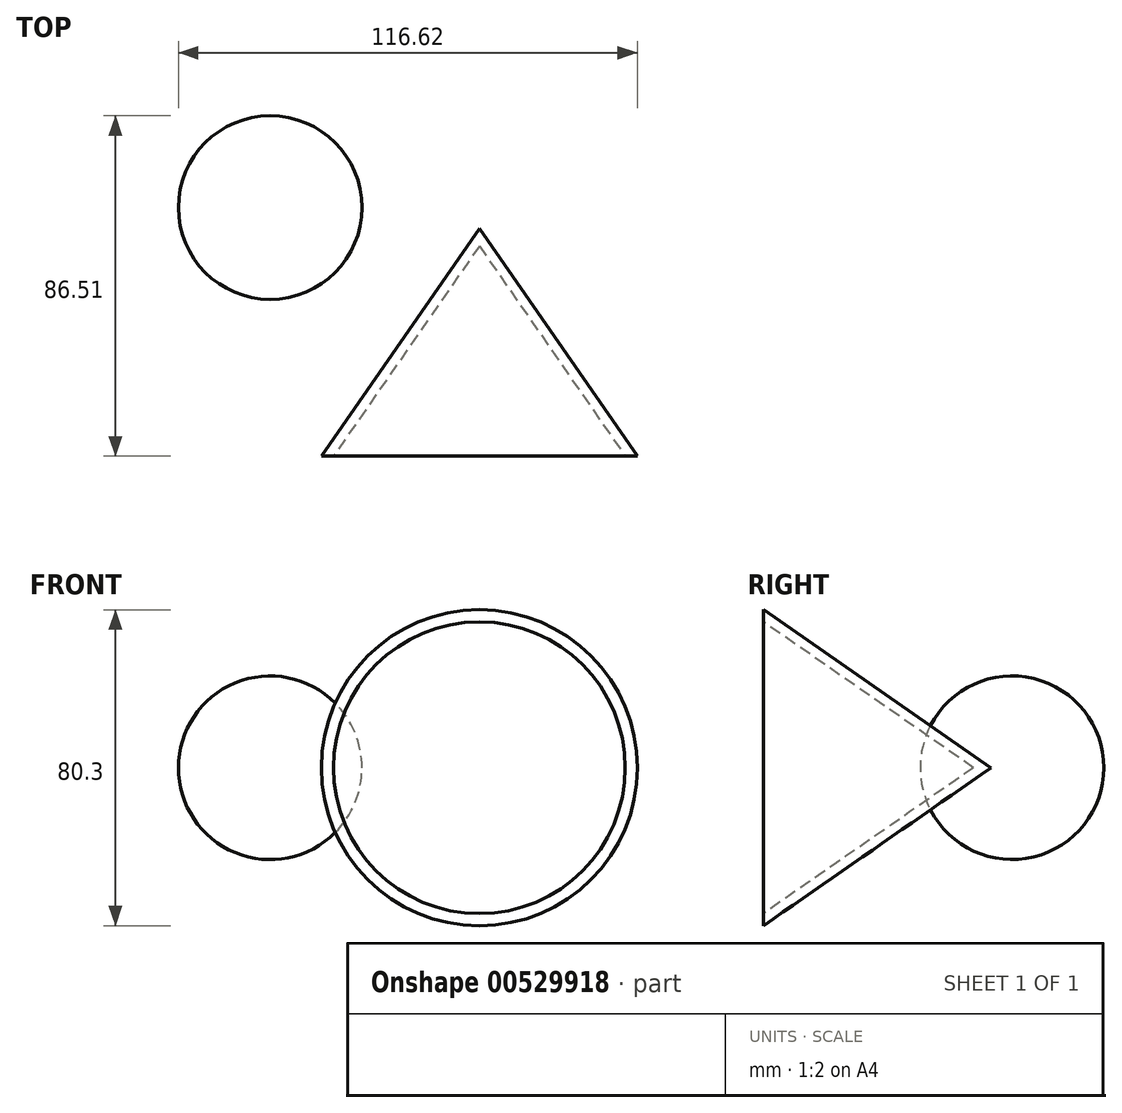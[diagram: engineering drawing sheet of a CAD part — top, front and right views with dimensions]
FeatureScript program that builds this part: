
annotation { "Feature Type Name" : "Feature", "Feature Type Description" : "" }
export const myFeature = defineFeature(function(context is Context, id is Id, definition is map)
    precondition{}
    {
        {
            var Q0;
            Q0=qCreatedBy(makeId("Top.planeOp"),FACE);
            var sketch = newSketch(context, id + "F0", { "sketchPlane" : qUnion([Q0])});
            skLineSegment(sketch, "E0", {"start": v(-46.65, 27.75) * mm, "end": v(0, 27.75) * mm});
            skArc(sketch, "E1", {"start": v(0, 27.75) * mm, "mid": v(-23.32, 51.08) * mm, "end": v(-46.65, 27.75) * mm});
            skSolve(sketch);
        }
        {
            var Q0;
            Q0=makeQuery(id+"F0.imprint","IMPRINT",FACE,{"disambiguationData":[TD([[makeQuery(id+"F0.imprint","IMPRINT",EDGE,{"derivedFrom":sQuery(id+"F0.wireOp",EDGE,"E0")}),1.0]])]});
            var Q1;
            Q1=sQuery(id+"F0.wireOp",EDGE,"E0");
            revolve(context, id + "F1", {"entities" : qUnion([Q0]), "axis" : qUnion([Q1]), "revolveType" : RevolveType.FULL});
        }
        {
            var Q0;
            Q0=qCreatedBy(makeId("Top.planeOp"),FACE);
            var sketch = newSketch(context, id + "F2", { "sketchPlane" : qUnion([Q0])});
            skLineSegment(sketch, "E2", {"start": v(29.82, 22.44) * mm, "end": v(29.82, -35.43) * mm});
            skLineSegment(sketch, "E3", {"start": v(-10.33, -35.43) * mm, "end": v(29.82, -35.43) * mm});
            skLineSegment(sketch, "E4", {"start": v(-10.33, -35.43) * mm, "end": v(29.82, 22.44) * mm});
            skSolve(sketch);
        }
        {
            var Q0;
            Q0=makeQuery(id+"F2.imprint","IMPRINT",FACE,{"disambiguationData":[TD([[makeQuery(id+"F2.imprint","IMPRINT",EDGE,{"derivedFrom":sQuery(id+"F2.wireOp",EDGE,"E2")}),-1.0]])]});
            var Q1;
            Q1=sQuery(id+"F2.wireOp",EDGE,"E2");
            revolve(context, id + "F3", {"entities" : qUnion([Q0]), "axis" : qUnion([Q1]), "revolveType" : RevolveType.FULL});
        }
        {
            var Q0;
            Q0=makeQuery(id+"F3.opRevolve","SWEPT_FACE",FACE,{"disambiguationData":[OSD([sQuery(id+"F2.wireOp",EDGE,"E3")])]});
            shell(context, id + "F4", {"entities" : qUnion([Q0]), "thickness" : 2.54 * mm});
        }
    });
